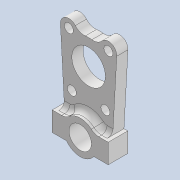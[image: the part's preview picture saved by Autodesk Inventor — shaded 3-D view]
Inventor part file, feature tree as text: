
AUTODESK INVENTOR PART (.ipt)
format: ipt  version: 2020 (Build 240168000, 168)  size: 257,024 bytes
history: native  units: mm
features: extrude x3, fillet x3, sketch x3, other x3, thicken_offset x2, reference x2, projected_geometry x2, chamfer x1
ambient origin geometry x8: Origin, YZ Plane, XZ Plane, XY Plane, X Axis, Y Axis, Z Axis, Center Point
bodies: Solid1 (feature_tree)
feature tree (19):
  extrude  "Extrusion1"  Depth=3.0mm
  extrude  "Extrusion2"  Depth=9.0mm
  fillet  "Fillet1"  Radius=4.0mm
  extrude  "Extrusion3"  Depth=10.0mm
  chamfer  "Chamfer1"  Distance=3.5mm
  fillet  "Fillet4"  Radius=1.5mm
  thicken_offset  "Thicken1"
  thicken_offset  "Thicken2"
  fillet  "Fillet5"  Radius=2.0mm
  sketch  "Sketch1"  dims[d0=6.0mm d1=3.0mm]
  reference  "Reference1"
  sketch  "Sketch2"  dims[d2=3.0mm d3=9.0mm d4=4.0mm]
  reference  "Reference2"
  projected_geometry  "Projected Loop1"
  sketch  "Sketch3"  dims[d5=3.5mm d6=10.0mm d7=3.5mm d8=0.0mm d9=1.5mm d10=0.0mm d11=2.0mm d14=1.75mm d15=2.0mm d16=10.0mm d17=0.0mm d18=0.5mm d19=2.0mm d20=45.0deg d21=1.0mm d22=0.5mm d23=0.5mm d24=0.5mm d25=0.5mm d26=0.5mm]
  projected_geometry  "Projected Loop2"
  parser-record x1  (decoder bookkeeping rows leaked as tree rows — omitted from the tree; the rows remain in map.json)
  other  "tip_ass_t1.iam"
  other  "pin_conn_2:1"
note: 1 file-system path scrubbed to <path> (originals preserved in map.json)
